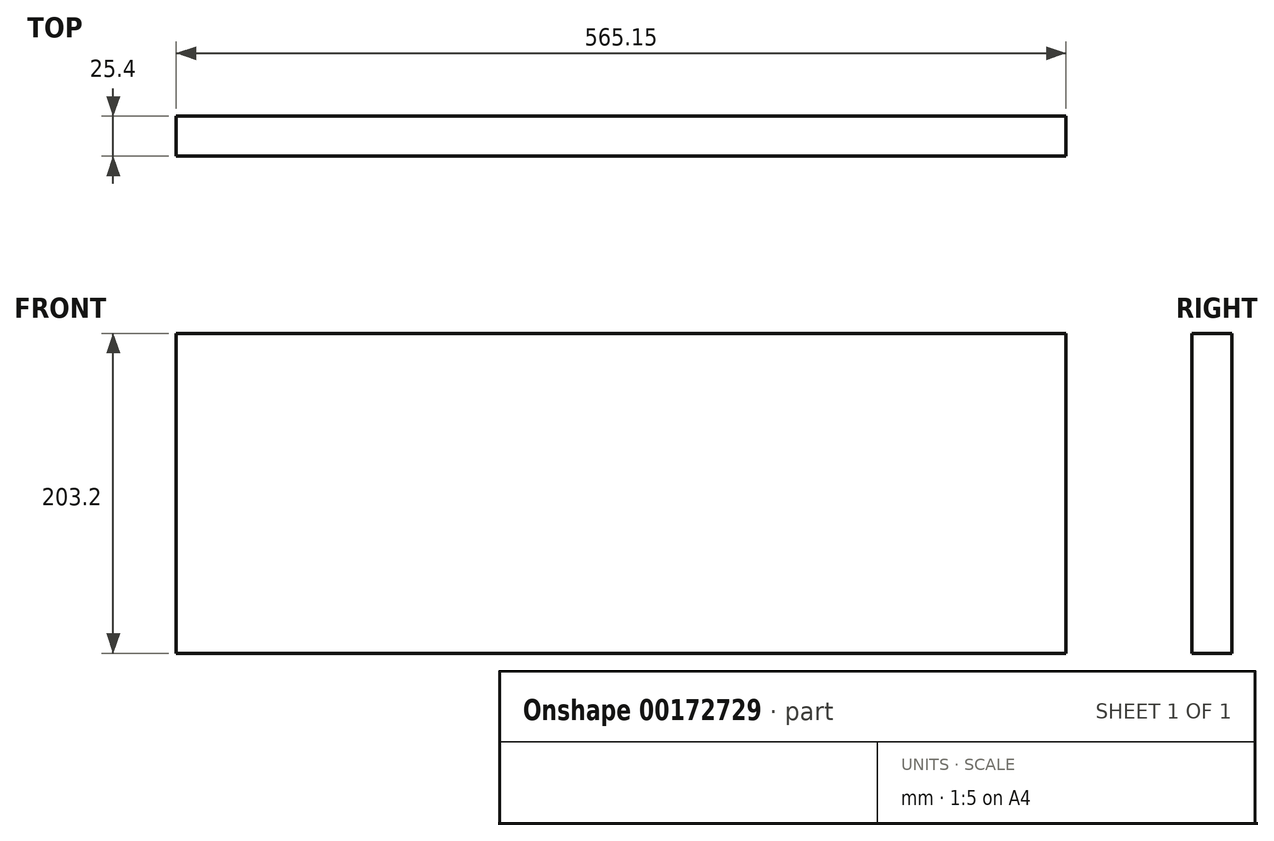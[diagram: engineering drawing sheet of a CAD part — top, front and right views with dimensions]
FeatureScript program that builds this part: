
annotation { "Feature Type Name" : "Feature", "Feature Type Description" : "" }
export const myFeature = defineFeature(function(context is Context, id is Id, definition is map)
    precondition{}
    {
        {
            var Q0;
            Q0=qCreatedBy(makeId("Front.planeOp"),FACE);
            var sketch = newSketch(context, id + "F0", { "sketchPlane" : qUnion([Q0])});
            skLineSegment(sketch, "E0.bottom", {"start": v(-305.79, 33.17) * mm, "end": v(259.36, 33.17) * mm});
            skLineSegment(sketch, "E0.top", {"start": v(-305.79, -170.03) * mm, "end": v(259.36, -170.03) * mm});
            skLineSegment(sketch, "E0.left", {"start": v(-305.79, 33.17) * mm, "end": v(-305.79, -170.03) * mm});
            skLineSegment(sketch, "E0.right", {"start": v(259.36, 33.17) * mm, "end": v(259.36, -170.03) * mm});
            skSolve(sketch);
        }
        {
            var Q0;
            Q0 = qSketchRegion(id + "F0", true);
            extrude(context, id + "F1", {"entities" : qUnion([Q0]), "depth" : 25.4 * mm});
        }
    });
